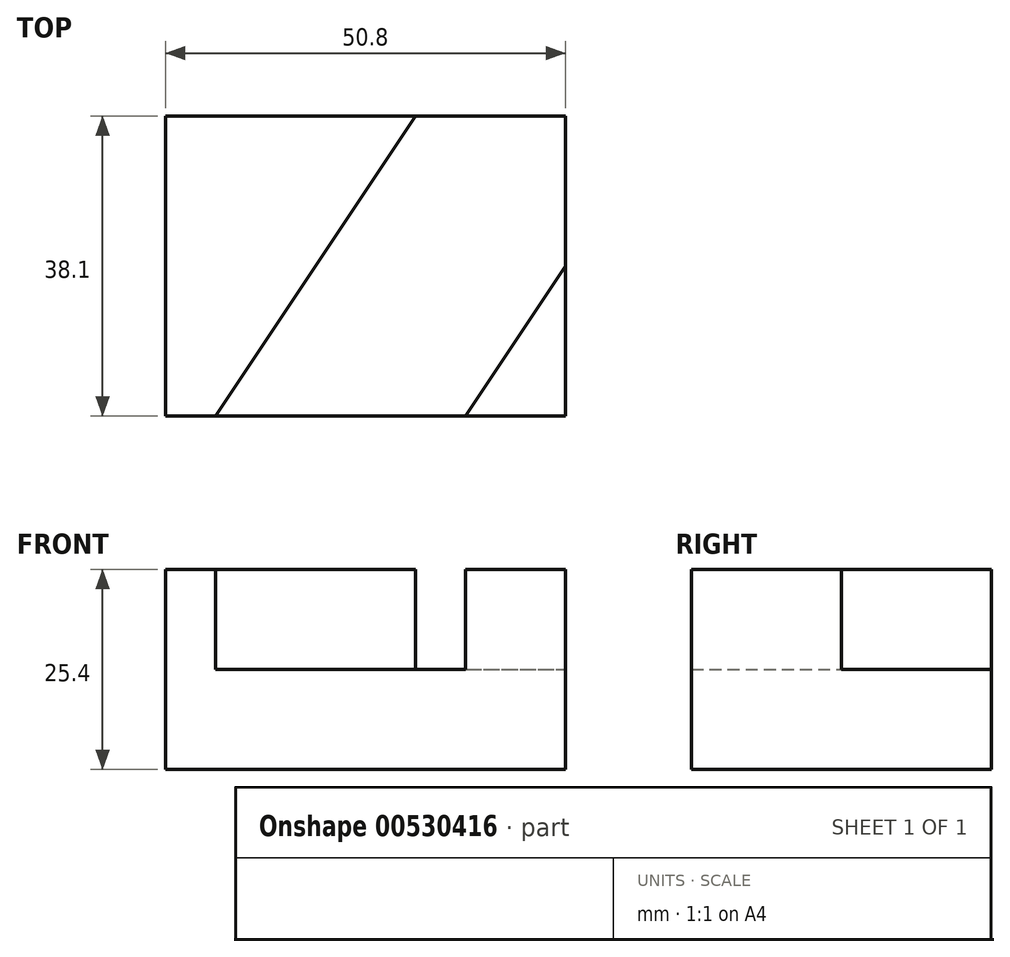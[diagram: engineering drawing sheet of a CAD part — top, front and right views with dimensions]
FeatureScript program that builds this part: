
annotation { "Feature Type Name" : "Feature", "Feature Type Description" : "" }
export const myFeature = defineFeature(function(context is Context, id is Id, definition is map)
    precondition{}
    {
        {
            var Q0;
            Q0=qCreatedBy(makeId("Top.planeOp"),FACE);
            var sketch = newSketch(context, id + "F0", { "sketchPlane" : qUnion([Q0])});
            skLineSegment(sketch, "E0", {"start": v(-33.68, 38.1) * mm, "end": v(-33.68, 0) * mm});
            skLineSegment(sketch, "E1", {"start": v(-33.68, 0) * mm, "end": v(17.12, 0) * mm});
            skLineSegment(sketch, "E2", {"start": v(-33.68, 38.1) * mm, "end": v(17.12, 38.1) * mm});
            skLineSegment(sketch, "E3", {"start": v(17.12, 38.1) * mm, "end": v(17.12, 0) * mm});
            skSolve(sketch);
        }
        {
            var Q0;
            Q0=makeQuery(id+"F0.imprint","IMPRINT",FACE,{"disambiguationData":[TD([[makeQuery(id+"F0.imprint","IMPRINT",EDGE,{"derivedFrom":sQuery(id+"F0.wireOp",EDGE,"E0")}),1.0]])]});
            extrude(context, id + "F1", {"entities" : qUnion([Q0]), "depth" : 12.7 * mm, "offsetDistance" : 25.4 * mm});
        }
        {
            var Q0;
            Q0=makeQuery(id+"F1.opExtrude","CAP_FACE",FACE,{"disambiguationData":[OSD([sQuery(id+"F0.wireOp",EDGE,"E0"),sQuery(id+"F0.wireOp",EDGE,"E1"),sQuery(id+"F0.wireOp",EDGE,"E2"),sQuery(id+"F0.wireOp",EDGE,"E3")])],"isStart":false});
            var sketch = newSketch(context, id + "F2", { "sketchPlane" : qUnion([Q0])});
            skLineSegment(sketch, "E4", {"start": v(-27.33, 0) * mm, "end": v(-1.93, 38.1) * mm});
            skLineSegment(sketch, "E5", {"start": v(4.42, 0) * mm, "end": v(17.12, 19.05) * mm});
            skSolve(sketch);
        }
        {
            var Q0;
            {var subQ0=sQuery(id+"F2.wireOp",EDGE,"E4");Q0=makeQuery(id+"F2.imprint","IMPRINT",FACE,{"disambiguationData":[TD([[makeQuery(id+"F2.imprint","IMPRINT",EDGE,{"derivedFrom":subQ0}),1.0]])]});}
            var Q1;
            {var subQ0=sQuery(id+"F2.wireOp",EDGE,"E5");Q1=makeQuery(id+"F2.imprint","IMPRINT",FACE,{"disambiguationData":[TD([[makeQuery(id+"F2.imprint","IMPRINT",EDGE,{"derivedFrom":subQ0}),-1.0]])]});}
            extrude(context, id + "F3", {"entities" : qUnion([Q0, Q1]), "operationType" : NewBodyOperationType.ADD, "depth" : 12.7 * mm, "offsetDistance" : 25.4 * mm});
        }
    });
